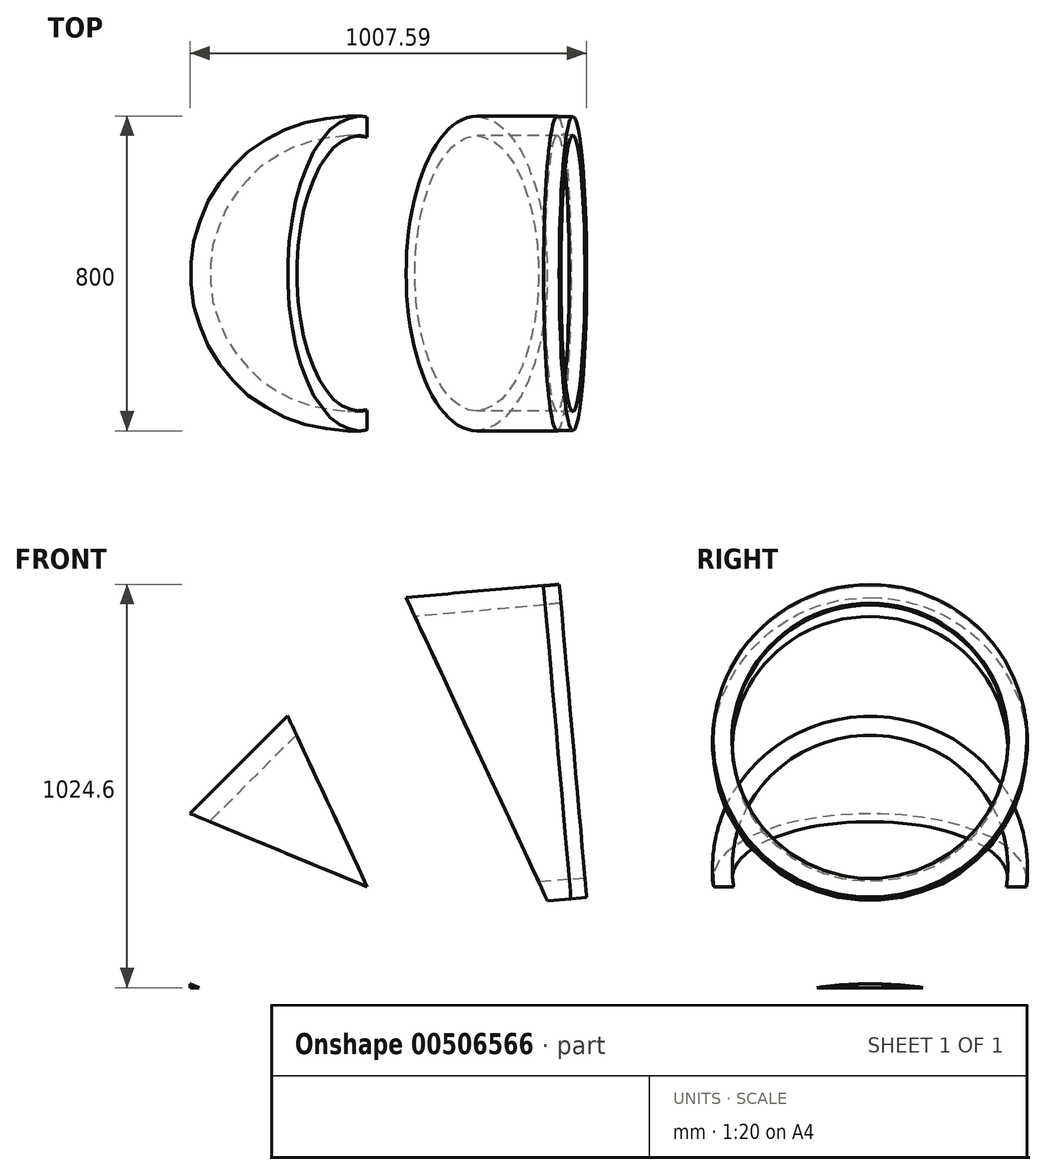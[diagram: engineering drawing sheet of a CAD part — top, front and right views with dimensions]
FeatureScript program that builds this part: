
annotation { "Feature Type Name" : "Feature", "Feature Type Description" : "" }
export const myFeature = defineFeature(function(context is Context, id is Id, definition is map)
    precondition{}
    {
        {
            var Q0;
            Q0=qCreatedBy(makeId("Front.planeOp"),FACE);
            var sketch = newSketch(context, id + "F0", { "sketchPlane" : qUnion([Q0])});
            skLineSegment(sketch, "E0", {"start": v(0, 0) * mm, "end": v(0, -525.84) * mm, "construction": true});
            skLineSegment(sketch, "E1", {"start": v(-400, -577) * mm, "end": v(-399, -577) * mm});
            skLineSegment(sketch, "E2", {"start": v(-399, -577) * mm, "end": v(-399, -537) * mm});
            skLineSegment(sketch, "E3", {"start": v(-399, -537) * mm, "end": v(-351, -537) * mm});
            skLineSegment(sketch, "E4", {"start": v(-351, -537) * mm, "end": v(-351, -577) * mm});
            skLineSegment(sketch, "E5", {"start": v(-351, -577) * mm, "end": v(-350, -577) * mm});
            skLineSegment(sketch, "E6", {"start": v(0, 0) * mm, "end": v(-753, -65.88) * mm, "construction": true});
            skLineSegment(sketch, "E7", {"start": v(-400, -577) * mm, "end": v(-400, -134.31) * mm});
            skLineSegment(sketch, "E8", {"start": v(-350, -577) * mm, "end": v(-350, -155.03) * mm});
            skLineSegment(sketch, "E9", {"start": v(0, 0) * mm, "end": v(735.4, 64.34) * mm, "construction": true});
            skLineSegment(sketch, "E10", {"start": v(502.46, 395.3) * mm, "end": v(502.37, 396.3) * mm});
            skLineSegment(sketch, "E11", {"start": v(502.37, 396.3) * mm, "end": v(542.22, 399.78) * mm});
            skLineSegment(sketch, "E12", {"start": v(542.22, 399.78) * mm, "end": v(538.04, 447.6) * mm});
            skLineSegment(sketch, "E13", {"start": v(538.04, 447.6) * mm, "end": v(498.19, 444.11) * mm});
            skLineSegment(sketch, "E14", {"start": v(498.19, 444.11) * mm, "end": v(498.1, 445.1) * mm});
            skLineSegment(sketch, "E15", {"start": v(498.1, 445.1) * mm, "end": v(148.87, 414.55) * mm});
            skLineSegment(sketch, "E16", {"start": v(-350, -155.03) * mm, "end": v(171.35, 366.33) * mm});
            skLineSegment(sketch, "E17", {"start": v(-350, -155.03) * mm, "end": v(-766.78, 17.61) * mm, "construction": true});
            skLineSegment(sketch, "E18", {"start": v(-350, -155.03) * mm, "end": v(-758.83, -155.03) * mm, "construction": true});
            skLineSegment(sketch, "E19", {"start": v(-350, -155.03) * mm, "end": v(-400, -134.31) * mm});
            skLineSegment(sketch, "E20", {"start": v(171.35, 366.33) * mm, "end": v(152.02, 809.06) * mm, "construction": true});
            skLineSegment(sketch, "E21", {"start": v(171.35, 366.33) * mm, "end": v(-12.7, 761.05) * mm, "construction": true});
            skLineSegment(sketch, "E22", {"start": v(171.35, 366.33) * mm, "end": v(148.87, 414.55) * mm});
            skLineSegment(sketch, "E23.trimOffspring", {"start": v(171.35, 366.33) * mm, "end": v(502.46, 395.3) * mm});
            skLineSegment(sketch, "E24", {"start": v(-400, -134.31) * mm, "end": v(148.87, 414.55) * mm});
            skLineSegment(sketch, "E25", {"start": v(-350, -155.03) * mm, "end": v(861.1, -656.68) * mm, "construction": true});
            skLineSegment(sketch, "E26", {"start": v(171.35, 366.33) * mm, "end": v(669.75, -702.48) * mm, "construction": true});
            skLineSegment(sketch, "E27", {"start": v(0, -300) * mm, "end": v(328.76, 28.76) * mm, "construction": true});
            skSolve(sketch);
        }
        {
            var Q0;
            Q0=qCreatedBy(makeId("Right.planeOp"),FACE);
            var sketch = newSketch(context, id + "F1", { "sketchPlane" : qUnion([Q0])});
            skLineSegment(sketch, "E28", {"start": v(288.35, -300) * mm, "end": v(-360.5, -300) * mm, "construction": true});
            skSolve(sketch);
        }
        {
            var Q0;
            Q0=sQuery(id+"F1.wireOp",EDGE,"E28");
            var Q1;
            Q1=sQuery(id+"F0.wireOp",EDGE,"E25");
            cPlane(context, id + "F2", {"entities" : qUnion([Q0, Q1]), "cplaneType" : CPlaneType.LINE_ANGLE, "offset" : 25 * mm, "angle" : 0 * degree, "width" : 150 * mm, "height" : 150 * mm});
        }
        {
            var Q0;
            Q0=sQuery(id+"F0.wireOp",EDGE,"E26");
            cPlane(context, id + "F3", {"entities" : qUnion([Q0]), "cplaneType" : CPlaneType.LINE_ANGLE, "offset" : 25 * mm, "angle" : 0 * degree, "width" : 150 * mm, "height" : 150 * mm});
        }
        {
            var Q0;
            Q0=qCreatedBy(id+"F2.planeOp",FACE);
            var sketch = newSketch(context, id + "F4", { "sketchPlane" : qUnion([Q0])});
            skLineSegment(sketch, "E29.bottom", {"start": v(-815.8, -791.8) * mm, "end": v(1036.86, -791.8) * mm});
            skLineSegment(sketch, "E29.top", {"start": v(-815.8, 744.83) * mm, "end": v(1036.86, 744.83) * mm});
            skLineSegment(sketch, "E29.left", {"start": v(-815.8, -791.8) * mm, "end": v(-815.8, 744.83) * mm});
            skLineSegment(sketch, "E29.right", {"start": v(1036.86, -791.8) * mm, "end": v(1036.86, 744.83) * mm});
            skSolve(sketch);
        }
        {
            var Q0;
            Q0=qCreatedBy(id+"F3.planeOp",FACE);
            var sketch = newSketch(context, id + "F5", { "sketchPlane" : qUnion([Q0])});
            skLineSegment(sketch, "E30.bottom", {"start": v(754.29, -977.32) * mm, "end": v(-876.24, -977.32) * mm});
            skLineSegment(sketch, "E30.top", {"start": v(754.29, 712.75) * mm, "end": v(-876.24, 712.75) * mm});
            skLineSegment(sketch, "E30.left", {"start": v(754.29, -977.32) * mm, "end": v(754.29, 712.75) * mm});
            skLineSegment(sketch, "E30.right", {"start": v(-876.24, -977.32) * mm, "end": v(-876.24, 712.75) * mm});
            skSolve(sketch);
        }
        {
            var Q0;
            Q0=makeQuery(id+"F0.imprint","IMPRINT",FACE,{"disambiguationData":[TD([[makeQuery(id+"F0.imprint","IMPRINT",EDGE,{"derivedFrom":sQuery(id+"F0.wireOp",EDGE,"E1")}),1.0]])]});
            var Q1;
            Q1=sQuery(id+"F0.wireOp",EDGE,"E0");
            revolve(context, id + "F6", {"entities" : qUnion([Q0]), "axis" : qUnion([Q1]), "revolveType" : RevolveType.FULL});
        }
        {
            var Q0;
            Q0=makeQuery(id+"F4.imprint","IMPRINT",FACE,{"disambiguationData":[TD([[makeQuery(id+"F4.imprint","IMPRINT",EDGE,{"derivedFrom":sQuery(id+"F4.wireOp",EDGE,"E29.bottom")}),1.0]])]});
            var Q1;
            Q1=makeQuery(id+"F6.opRevolve","SWEPT_BODY",BODY,{"disambiguationData":[OSD([sQuery(id+"F0.wireOp",EDGE,"E1"),sQuery(id+"F0.wireOp",EDGE,"E2"),sQuery(id+"F0.wireOp",EDGE,"E3"),sQuery(id+"F0.wireOp",EDGE,"E4"),sQuery(id+"F0.wireOp",EDGE,"E5"),sQuery(id+"F0.wireOp",EDGE,"E7"),sQuery(id+"F0.wireOp",EDGE,"E8"),sQuery(id+"F0.wireOp",EDGE,"E19")])]});
            extrude(context, id + "F7", {"entities" : qUnion([Q0]), "operationType" : NewBodyOperationType.REMOVE, "endBoundEntityBody" : qUnion([Q1]), "depth" : 400 * mm});
        }
        {
            var Q0;
            Q0=makeQuery(id+"F0.imprint","IMPRINT",FACE,{"disambiguationData":[TD([[makeQuery(id+"F0.imprint","IMPRINT",EDGE,{"derivedFrom":sQuery(id+"F0.wireOp",EDGE,"E16")}),1.0]])]});
            var Q1;
            Q1=sQuery(id+"F0.wireOp",EDGE,"E27");
            revolve(context, id + "F8", {"entities" : qUnion([Q0]), "axis" : qUnion([Q1]), "revolveType" : RevolveType.FULL});
        }
        {
            var Q0;
            Q0=makeQuery(id+"F4.imprint","IMPRINT",FACE,{"disambiguationData":[TD([[makeQuery(id+"F4.imprint","IMPRINT",EDGE,{"derivedFrom":sQuery(id+"F4.wireOp",EDGE,"E29.bottom")}),1.0]])]});
            extrude(context, id + "F9", {"entities" : qUnion([Q0]), "operationType" : NewBodyOperationType.REMOVE, "oppositeDirection" : true, "depth" : 400 * mm});
        }
        {
            var Q0;
            Q0=makeQuery(id+"F5.imprint","IMPRINT",FACE,{"disambiguationData":[TD([[makeQuery(id+"F5.imprint","IMPRINT",EDGE,{"derivedFrom":sQuery(id+"F5.wireOp",EDGE,"E30.bottom")}),-1.0]])]});
            extrude(context, id + "F10", {"entities" : qUnion([Q0]), "operationType" : NewBodyOperationType.REMOVE, "oppositeDirection" : true, "depth" : 400 * mm});
        }
        {
            var Q0;
            Q0=makeQuery(id+"F0.imprint","IMPRINT",FACE,{"disambiguationData":[TD([[makeQuery(id+"F0.imprint","IMPRINT",EDGE,{"derivedFrom":sQuery(id+"F0.wireOp",EDGE,"E10")}),1.0]])]});
            var Q1;
            Q1=sQuery(id+"F0.wireOp",EDGE,"E9");
            revolve(context, id + "F11", {"entities" : qUnion([Q0]), "axis" : qUnion([Q1]), "revolveType" : RevolveType.FULL});
        }
        {
            var Q0;
            Q0=makeQuery(id+"F5.imprint","IMPRINT",FACE,{"disambiguationData":[TD([[makeQuery(id+"F5.imprint","IMPRINT",EDGE,{"derivedFrom":sQuery(id+"F5.wireOp",EDGE,"E30.bottom")}),-1.0]])]});
            extrude(context, id + "F12", {"entities" : qUnion([Q0]), "operationType" : NewBodyOperationType.REMOVE, "depth" : 400 * mm});
        }
    });
